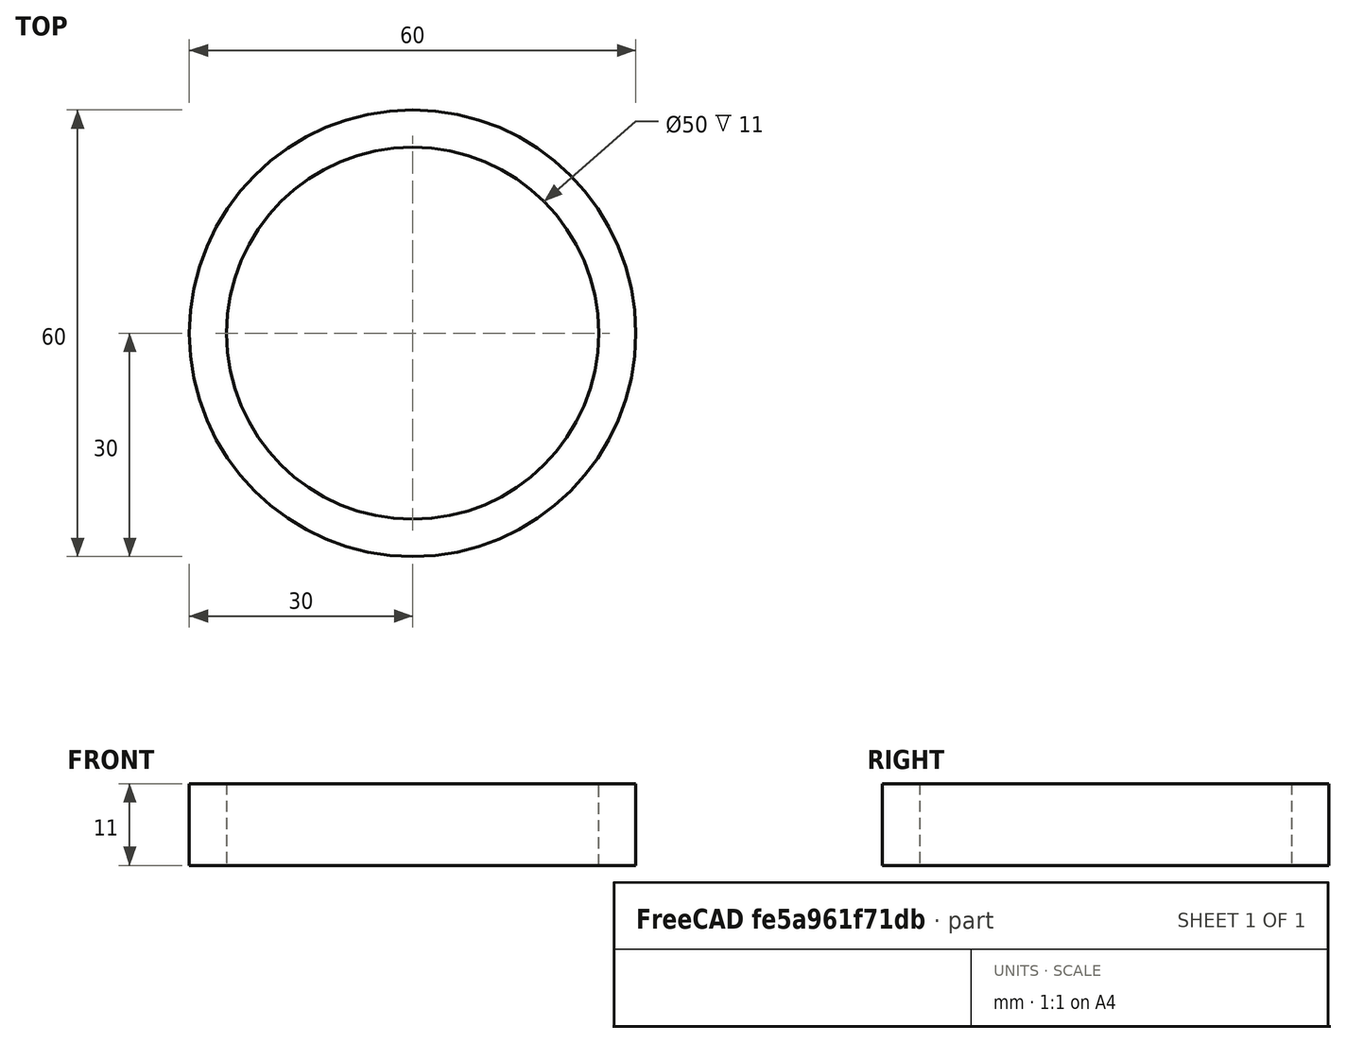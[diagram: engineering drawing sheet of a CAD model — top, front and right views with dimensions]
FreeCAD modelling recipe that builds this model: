
FCSTD DOCUMENT  (FreeCAD 0.19R24276 (Git))
Label: Ring_45x75x11_IN
License: All rights reserved
LicenseURL: http://en.wikipedia.org/wiki/All_rights_reserved
objects: Sketcher::SketchObject×1, PartDesign::Pad×1, PartDesign::Body×1
note: 4 computed .brp shape members not serialized (recipe doc carries the construction recipe); baked Part::Feature solids carry a one-line shape summary decoded from their .brp

FEATURE [Sketcher::SketchObject] Sketch
  FullyConstrained = true
  MapMode = 5
  Support = -> [XY_Plane]
  sketch-geometry (2):
    g0: Circle CenterX=0 CenterY=0 CenterZ=0 NormalX=0 NormalY=0 NormalZ=1 AngleXU=0 Radius=30
    g1: Circle CenterX=0 CenterY=0 CenterZ=0 NormalX=0 NormalY=0 NormalZ=1 AngleXU=0 Radius=25
  constraints (4):
    c: Coincident(g1,g0)
    c: Diameter(g1) = 50
    c: Diameter(g0) = 60
    c: Coincident(g0,g-1)
FEATURE [PartDesign::Pad] Pad
  Direction = (1,1,1)
  Length = 11
  Length2 = 100
  Profile = -> Sketch
  Type = 0
FEATURE [PartDesign::Body] Body  label="Body_ring_in"
  Group = -> [Sketch,Pad]
  Origin = -> Origin
  Tip = -> Pad
